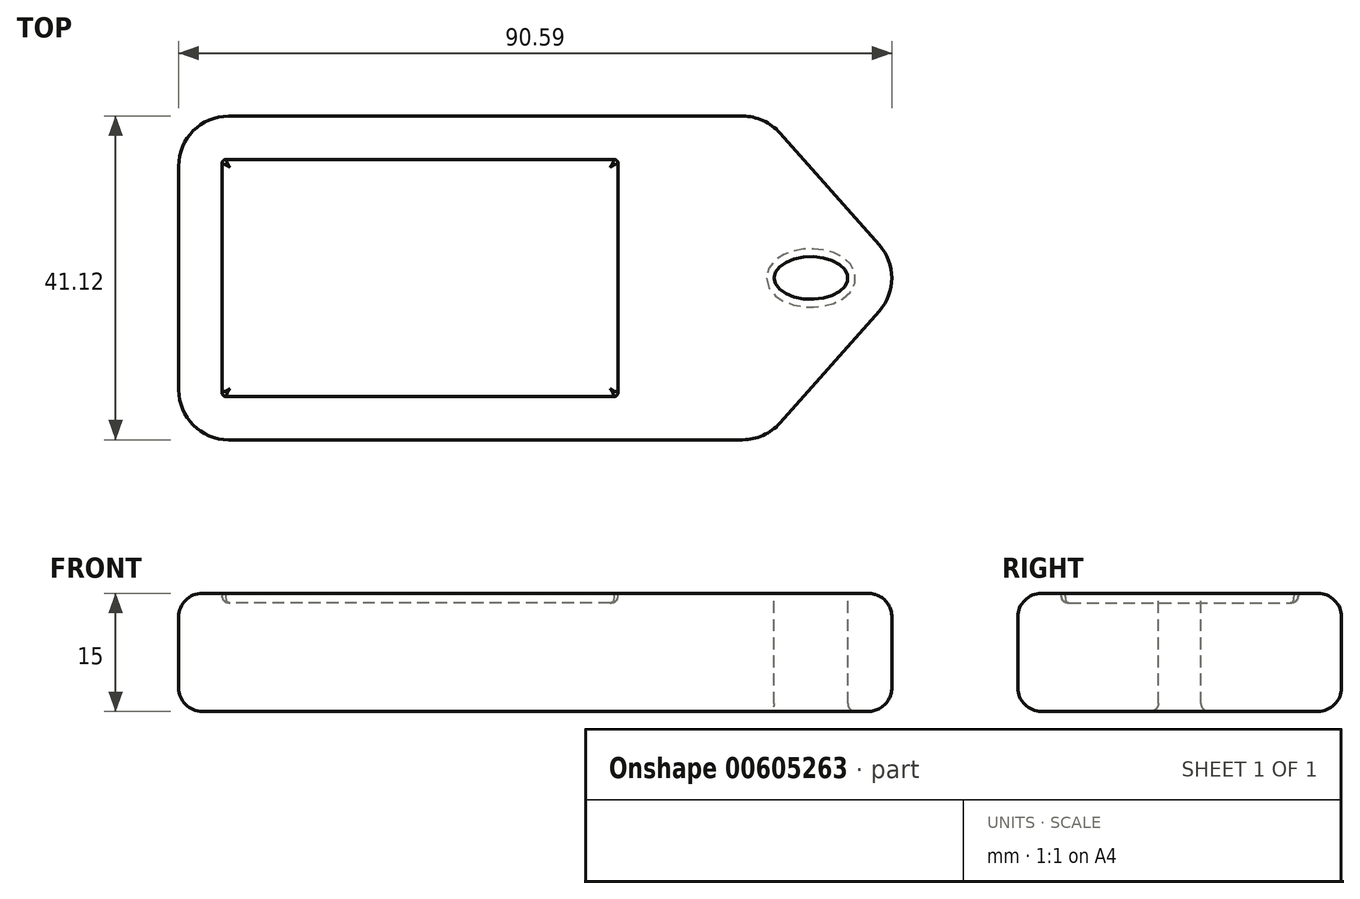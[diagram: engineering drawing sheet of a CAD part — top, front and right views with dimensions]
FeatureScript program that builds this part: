
annotation { "Feature Type Name" : "Feature", "Feature Type Description" : "" }
export const myFeature = defineFeature(function(context is Context, id is Id, definition is map)
    precondition{}
    {
        {
            var Q0;
            Q0=qCreatedBy(makeId("Top.planeOp"),FACE);
            var sketch = newSketch(context, id + "F0", { "sketchPlane" : qUnion([Q0])});
            skLineSegment(sketch, "E0.bottom", {"start": v(-32.64, -20.56) * mm, "end": v(32.64, -20.56) * mm});
            skLineSegment(sketch, "E0.top", {"start": v(-32.64, 20.56) * mm, "end": v(32.64, 20.56) * mm});
            skLineSegment(sketch, "E0.left", {"start": v(-39, -14.2) * mm, "end": v(-39, 14.2) * mm});
            skPoint(sketch, "E0.middle", {"position": v(0, 0) * mm});
            skPoint(sketch, "E1.visualSharp", {"position": v(-39, 20.56) * mm});
            skArc(sketch, "E1.filletArc", {"start": v(-32.64, 20.56) * mm, "mid": v(-37.13, 18.7) * mm, "end": v(-39, 14.2) * mm});
            skPoint(sketch, "E2.visualSharp", {"position": v(-39, -20.56) * mm});
            skArc(sketch, "E2.filletArc", {"start": v(-39, -14.2) * mm, "mid": v(-37.13, -18.7) * mm, "end": v(-32.64, -20.56) * mm});
            skPoint(sketch, "E3.visualSharp", {"position": v(39, 20.56) * mm});
            skArc(sketch, "E3.filletArc", {"start": v(37.4, 18.42) * mm, "mid": v(35.24, 20) * mm, "end": v(32.64, 20.56) * mm});
            skPoint(sketch, "E4.visualSharp", {"position": v(39, -20.56) * mm});
            skArc(sketch, "E4.filletArc", {"start": v(32.64, -20.56) * mm, "mid": v(35.24, -20) * mm, "end": v(37.4, -18.42) * mm});
            skLineSegment(sketch, "E5", {"start": v(50, 4.22) * mm, "end": v(37.13, 18.71) * mm});
            skPoint(sketch, "E5.endSnap0", {"position": v(37.13, 18.7) * mm});
            skLineSegment(sketch, "E6", {"start": v(50, -4.22) * mm, "end": v(37.4, -18.42) * mm});
            skPoint(sketch, "E7.orphan", {"position": v(35.5, -20.56) * mm});
            skPoint(sketch, "E8.visualSharp", {"position": v(53.74, 0) * mm});
            skArc(sketch, "E8.filletArc", {"start": v(50, -4.22) * mm, "mid": v(51.6, 0) * mm, "end": v(50, 4.22) * mm});
            skSolve(sketch);
        }
        {
            var Q0;
            Q0 = qSketchRegion(id + "F0", true);
            extrude(context, id + "F1", {"entities" : qUnion([Q0]), "depth" : 15 * mm, "offsetDistance" : 25.4 * mm});
        }
        {
            var Q0;
            Q0=makeQuery(id+"F1.opExtrude","CAP_EDGE",EDGE,{"disambiguationData":[OSD([sQuery(id+"F0.wireOp",EDGE,"E0.bottom")])],"isStart":false});
            var Q1;
            Q1=makeQuery(id+"F1.opExtrude","CAP_EDGE",EDGE,{"disambiguationData":[OSD([sQuery(id+"F0.wireOp",EDGE,"E0.bottom")])],"isStart":true});
            fillet(context, id + "F2", {"entities" : qUnion([Q0, Q1]), "radius" : 3 * mm, "tangentPropagation" : true, "allowEdgeOverflow" : false});
        }
        {
            var Q0;
            Q0=makeQuery(id+"F1.opExtrude","CAP_FACE",FACE,{"disambiguationData":[OSD([sQuery(id+"F0.wireOp",EDGE,"E0.bottom"),sQuery(id+"F0.wireOp",EDGE,"E0.top"),sQuery(id+"F0.wireOp",EDGE,"E0.left"),sQuery(id+"F0.wireOp",EDGE,"E1.filletArc"),sQuery(id+"F0.wireOp",EDGE,"E2.filletArc"),sQuery(id+"F0.wireOp",EDGE,"E3.filletArc"),sQuery(id+"F0.wireOp",EDGE,"E4.filletArc"),sQuery(id+"F0.wireOp",EDGE,"E5"),sQuery(id+"F0.wireOp",EDGE,"E6"),sQuery(id+"F0.wireOp",EDGE,"E8.filletArc")])],"isStart":false});
            var sketch = newSketch(context, id + "F3", { "sketchPlane" : qUnion([Q0])});
            skLineSegment(sketch, "E9.bottom", {"start": v(-33, 15.06) * mm, "end": v(16.32, 15.06) * mm});
            skLineSegment(sketch, "E9.top", {"start": v(-33, -15.06) * mm, "end": v(16.32, -15.06) * mm});
            skLineSegment(sketch, "E9.left", {"start": v(-33.5, 14.56) * mm, "end": v(-33.5, -14.56) * mm});
            skLineSegment(sketch, "E9.right", {"start": v(16.82, 14.56) * mm, "end": v(16.82, -14.56) * mm});
            skPoint(sketch, "E10.visualSharp", {"position": v(-33.5, 15.06) * mm});
            skArc(sketch, "E10.filletArc", {"start": v(-33, 15.06) * mm, "mid": v(-33.34, 14.9) * mm, "end": v(-33.5, 14.56) * mm});
            skPoint(sketch, "E11.visualSharp", {"position": v(-33.5, -15.06) * mm});
            skArc(sketch, "E11.filletArc", {"start": v(-33.5, -14.56) * mm, "mid": v(-33.34, -14.9) * mm, "end": v(-33, -15.06) * mm});
            skPoint(sketch, "E12.visualSharp", {"position": v(16.82, -15.06) * mm});
            skArc(sketch, "E12.filletArc", {"start": v(16.32, -15.06) * mm, "mid": v(16.68, -14.9) * mm, "end": v(16.82, -14.56) * mm});
            skPoint(sketch, "E13.visualSharp", {"position": v(16.82, 15.06) * mm});
            skArc(sketch, "E13.filletArc", {"start": v(16.82, 14.56) * mm, "mid": v(16.68, 14.9) * mm, "end": v(16.32, 15.06) * mm});
            skSolve(sketch);
        }
        {
            var Q0;
            Q0=makeQuery(id+"F3.imprint","IMPRINT",FACE,{"disambiguationData":[TD([[makeQuery(id+"F3.imprint","IMPRINT",EDGE,{"derivedFrom":sQuery(id+"F3.wireOp",EDGE,"E9.bottom")}),-1.0]])]});
            extrude(context, id + "F4", {"entities" : qUnion([Q0]), "operationType" : NewBodyOperationType.REMOVE, "oppositeDirection" : true, "depth" : 1.2 * mm, "offsetDistance" : 25 * mm});
        }
        {
            var Q0;
            Q0=makeQuery(id+"F4.boolean.opBoolean","COPY",EDGE,{"derivedFrom":makeQuery(id+"F4.opExtrude","CAP_EDGE",EDGE,{"disambiguationData":[OSD([sQuery(id+"F3.wireOp",EDGE,"E9.bottom")])],"isStart":false})});
            fillet(context, id + "F5", {"entities" : qUnion([Q0]), "radius" : 1 * mm, "tangentPropagation" : true, "rho" : 0.5, "crossSection" : FilletCrossSection.CONIC, "allowEdgeOverflow" : false});
        }
        {
            var Q0;
            Q0=makeQuery(id+"F1.opExtrude","CAP_FACE",FACE,{"disambiguationData":[OSD([sQuery(id+"F0.wireOp",EDGE,"E0.bottom"),sQuery(id+"F0.wireOp",EDGE,"E0.top"),sQuery(id+"F0.wireOp",EDGE,"E0.left"),sQuery(id+"F0.wireOp",EDGE,"E1.filletArc"),sQuery(id+"F0.wireOp",EDGE,"E2.filletArc"),sQuery(id+"F0.wireOp",EDGE,"E3.filletArc"),sQuery(id+"F0.wireOp",EDGE,"E4.filletArc"),sQuery(id+"F0.wireOp",EDGE,"E5"),sQuery(id+"F0.wireOp",EDGE,"E6"),sQuery(id+"F0.wireOp",EDGE,"E8.filletArc")])],"isStart":false});
            var sketch = newSketch(context, id + "F6", { "sketchPlane" : qUnion([Q0])});
            skEllipse(sketch, "E14", {"center": v(41.33, 0) * mm, "majorRadius": 4.67 * mm, "minorRadius": 2.7 * mm, "majorAxis": v(-1, 0)});
            skSolve(sketch);
        }
        {
            var Q0;
            Q0=makeQuery(id+"F6.imprint","IMPRINT",FACE,{"disambiguationData":[TD([[makeQuery(id+"F6.imprint","IMPRINT",EDGE,{"derivedFrom":sQuery(id+"F6.wireOp",EDGE,"E14")}),1.0]])]});
            extrude(context, id + "F7", {"entities" : qUnion([Q0]), "operationType" : NewBodyOperationType.REMOVE, "oppositeDirection" : true, "depth" : 25 * mm, "offsetDistance" : 25 * mm});
        }
        {
            var Q0;
            Q0=makeQuery(id+"F7.boolean.opBoolean","COPY",EDGE,{"derivedFrom":makeQuery(id+"F7.opExtrude","CAP_EDGE",EDGE,{"disambiguationData":[OSD([sQuery(id+"F6.wireOp",EDGE,"E14")])],"isStart":true})});
            var Q1;
            Q1=makeQuery(id+"F7.boolean.opBoolean","INTERSECT",EDGE,{"derivedFrom":[makeQuery(id+"F1.opExtrude","CAP_FACE",FACE,{"disambiguationData":[OSD([sQuery(id+"F0.wireOp",EDGE,"E0.bottom"),sQuery(id+"F0.wireOp",EDGE,"E0.top"),sQuery(id+"F0.wireOp",EDGE,"E0.left"),sQuery(id+"F0.wireOp",EDGE,"E1.filletArc"),sQuery(id+"F0.wireOp",EDGE,"E2.filletArc"),sQuery(id+"F0.wireOp",EDGE,"E3.filletArc"),sQuery(id+"F0.wireOp",EDGE,"E4.filletArc"),sQuery(id+"F0.wireOp",EDGE,"E5"),sQuery(id+"F0.wireOp",EDGE,"E6"),sQuery(id+"F0.wireOp",EDGE,"E8.filletArc")])],"isStart":true}),makeQuery(id+"F7.opExtrude","SWEPT_FACE",FACE,{"disambiguationData":[OSD([sQuery(id+"F6.wireOp",EDGE,"E14")])]})]});
            fillet(context, id + "F8", {"entities" : qUnion([Q0, Q1]), "radius" : 1 * mm, "tangentPropagation" : true, "allowEdgeOverflow" : false});
        }
    });
